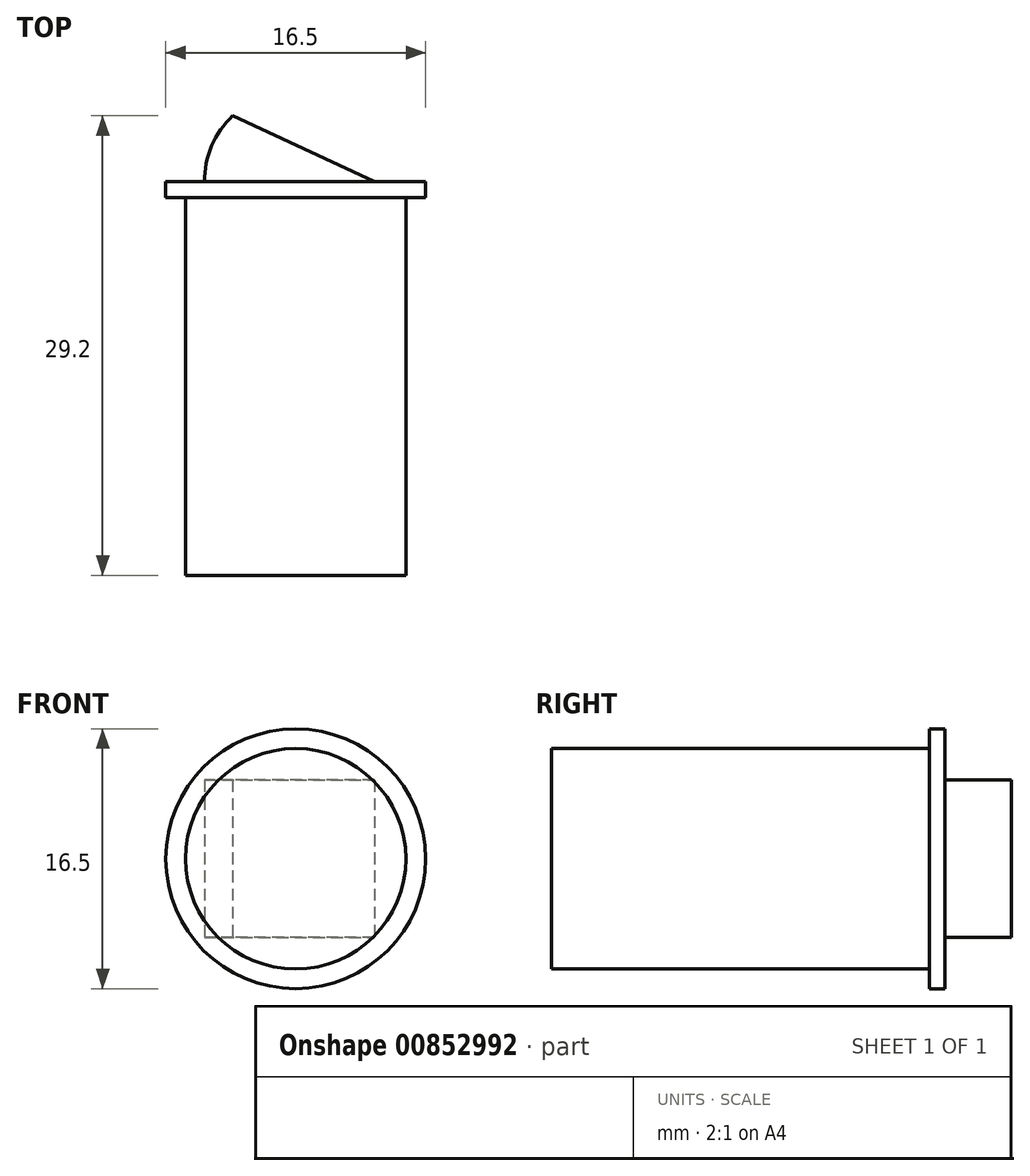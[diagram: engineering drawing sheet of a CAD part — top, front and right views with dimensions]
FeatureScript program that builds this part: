
annotation { "Feature Type Name" : "Feature", "Feature Type Description" : "" }
export const myFeature = defineFeature(function(context is Context, id is Id, definition is map)
    precondition{}
    {
        {
            var Q0;
            Q0=qCreatedBy(makeId("Front.planeOp"),FACE);
            var sketch = newSketch(context, id + "F0", { "sketchPlane" : qUnion([Q0])});
            skCircle(sketch, "E0", {"center": v(0, 0) * mm, "radius": 8.25 * mm});
            skSolve(sketch);
        }
        {
            var Q0;
            Q0=makeQuery(id+"F0.imprint","IMPRINT",FACE,{"disambiguationData":[TD([[makeQuery(id+"F0.imprint","IMPRINT",EDGE,{"derivedFrom":sQuery(id+"F0.wireOp",EDGE,"E0")}),1.0]])]});
            extrude(context, id + "F1", {"entities" : qUnion([Q0]), "depth" : 1 * mm, "offsetDistance" : 25 * mm});
        }
        {
            var Q0;
            Q0=qCreatedBy(makeId("Front.planeOp"),FACE);
            var sketch = newSketch(context, id + "F2", { "sketchPlane" : qUnion([Q0])});
            skCircle(sketch, "E1", {"center": v(0, 0) * mm, "radius": 7 * mm});
            skSolve(sketch);
        }
        {
            var Q0;
            Q0 = qSketchRegion(id + "F2", true);
            extrude(context, id + "F3", {"entities" : qUnion([Q0]), "operationType" : NewBodyOperationType.ADD, "depth" : 25 * mm, "offsetDistance" : 25 * mm});
        }
        {
            var Q0;
            Q0=qCreatedBy(makeId("Top.planeOp"),FACE);
            var sketch = newSketch(context, id + "F4", { "sketchPlane" : qUnion([Q0])});
            skLineSegment(sketch, "E2", {"start": v(-5.8, 0) * mm, "end": v(5, 0) * mm});
            skLineSegment(sketch, "E3", {"start": v(5, 0) * mm, "end": v(-4, 4.2) * mm});
            skArc(sketch, "E4", {"start": v(-4, 4.2) * mm, "mid": v(-5.33, 2.28) * mm, "end": v(-5.8, 0) * mm});
            skSolve(sketch);
        }
        {
            var Q0;
            Q0=makeQuery(id+"F4.imprint","IMPRINT",FACE,{"disambiguationData":[TD([[makeQuery(id+"F4.imprint","IMPRINT",EDGE,{"derivedFrom":sQuery(id+"F4.wireOp",EDGE,"E2")}),1.0]])]});
            extrude(context, id + "F5", {"entities" : qUnion([Q0]), "operationType" : NewBodyOperationType.ADD, "depth" : 10 * mm, "offsetDistance" : 25 * mm, "symmetric" : true});
        }
    });
